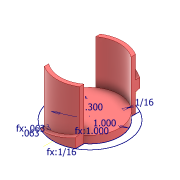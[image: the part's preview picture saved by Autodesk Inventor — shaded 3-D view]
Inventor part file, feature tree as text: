
AUTODESK INVENTOR PART (.ipt)
format: ipt  version: 2020.4 (Build 244396000, 396)  size: 189,440 bytes
history: native  units: in
note: dims shown in document units (in); Inventor stores cm internally (conversion verified against a paired STEP export)
features: extrude x3, sketch x2, helix x1
ambient origin geometry x8: Origin, YZ Plane, XZ Plane, XY Plane, X Axis, Y Axis, Z Axis, Center Point
bodies: Body1 (feature_tree)
feature tree (6):
  sketch  "Sketch1"  dims[d0=1.0in d1=0.1667in]
  extrude  "Extrusion3"  Depth=0.1667in
  extrude  "Extrusion4"  Depth=0.125in TaperAngle=0.0deg
  sketch  "Sketch2"  dims[d6=0.875in d7=0.0in d8=0.125in d9=0.0in d10=0.0625in d11=0.0625in d12=0.3in d13=0.0625in d14=1.0in d15=1.0in d16=0.2953in d17=0.0in d18=90.0deg d19=90.0deg d20=0.0in d21=0.0in d22=0.0625in d23=0.0625in d24=1.0in d25=1.0in d26=0.0in]
  helix  "Coil1"  [1 undecoded]
  extrude  "Extrusion5"  Depth=0.0625in
note: 1 required parameter value undecoded (feature->parameter linkage not recoverable at this tier; creation-order binding heuristic only, values carry confidence <= 0.55)
